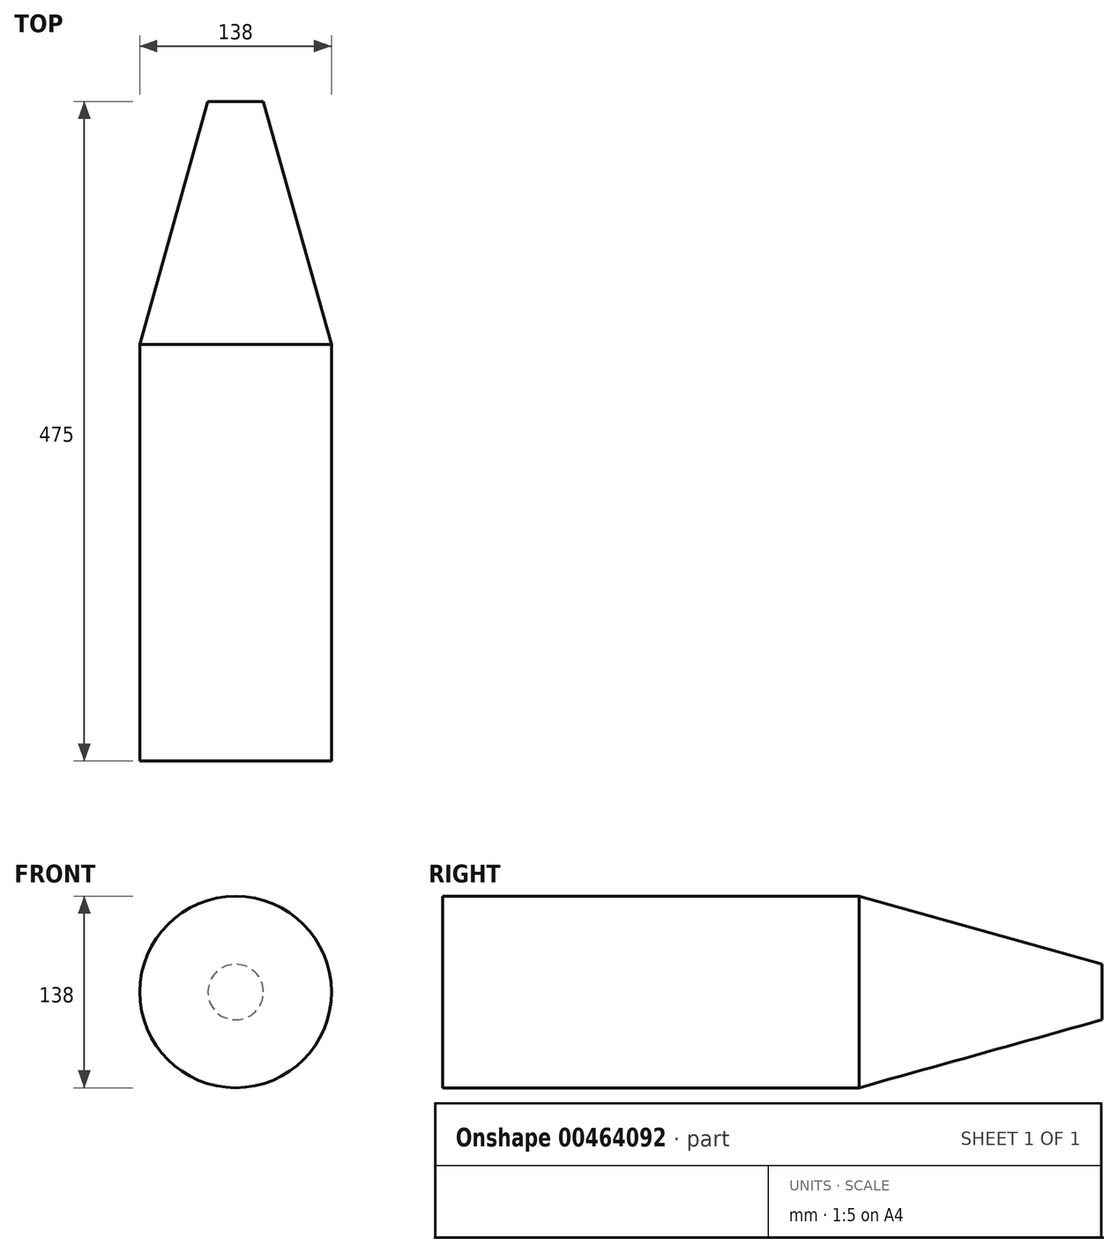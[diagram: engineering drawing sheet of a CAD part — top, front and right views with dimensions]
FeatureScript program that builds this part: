
annotation { "Feature Type Name" : "Feature", "Feature Type Description" : "" }
export const myFeature = defineFeature(function(context is Context, id is Id, definition is map)
    precondition{}
    {
        {
            var Q0;
            Q0=qCreatedBy(makeId("Right.planeOp"),FACE);
            var sketch = newSketch(context, id + "F0", { "sketchPlane" : qUnion([Q0])});
            skLineSegment(sketch, "E0", {"start": v(0, 0) * mm, "end": v(0, 69) * mm});
            skLineSegment(sketch, "E1", {"start": v(0, 69) * mm, "end": v(300, 69) * mm});
            skLineSegment(sketch, "E2", {"start": v(300, 69) * mm, "end": v(475, 20) * mm});
            skLineSegment(sketch, "E3", {"start": v(475, 20) * mm, "end": v(475, 0) * mm});
            skLineSegment(sketch, "E4", {"start": v(0, 0) * mm, "end": v(475, 0) * mm});
            skPoint(sketch, "E5.visualSharp", {"position": v(475, 20) * mm});
            skSolve(sketch);
        }
        {
            var Q0;
            Q0 = qSketchRegion(id + "F0", true);
            var Q1;
            Q1=sQuery(id+"F0.wireOp",EDGE,"E4");
            revolve(context, id + "F1", {"entities" : qUnion([Q0]), "axis" : qUnion([Q1]), "revolveType" : RevolveType.FULL});
        }
    });
